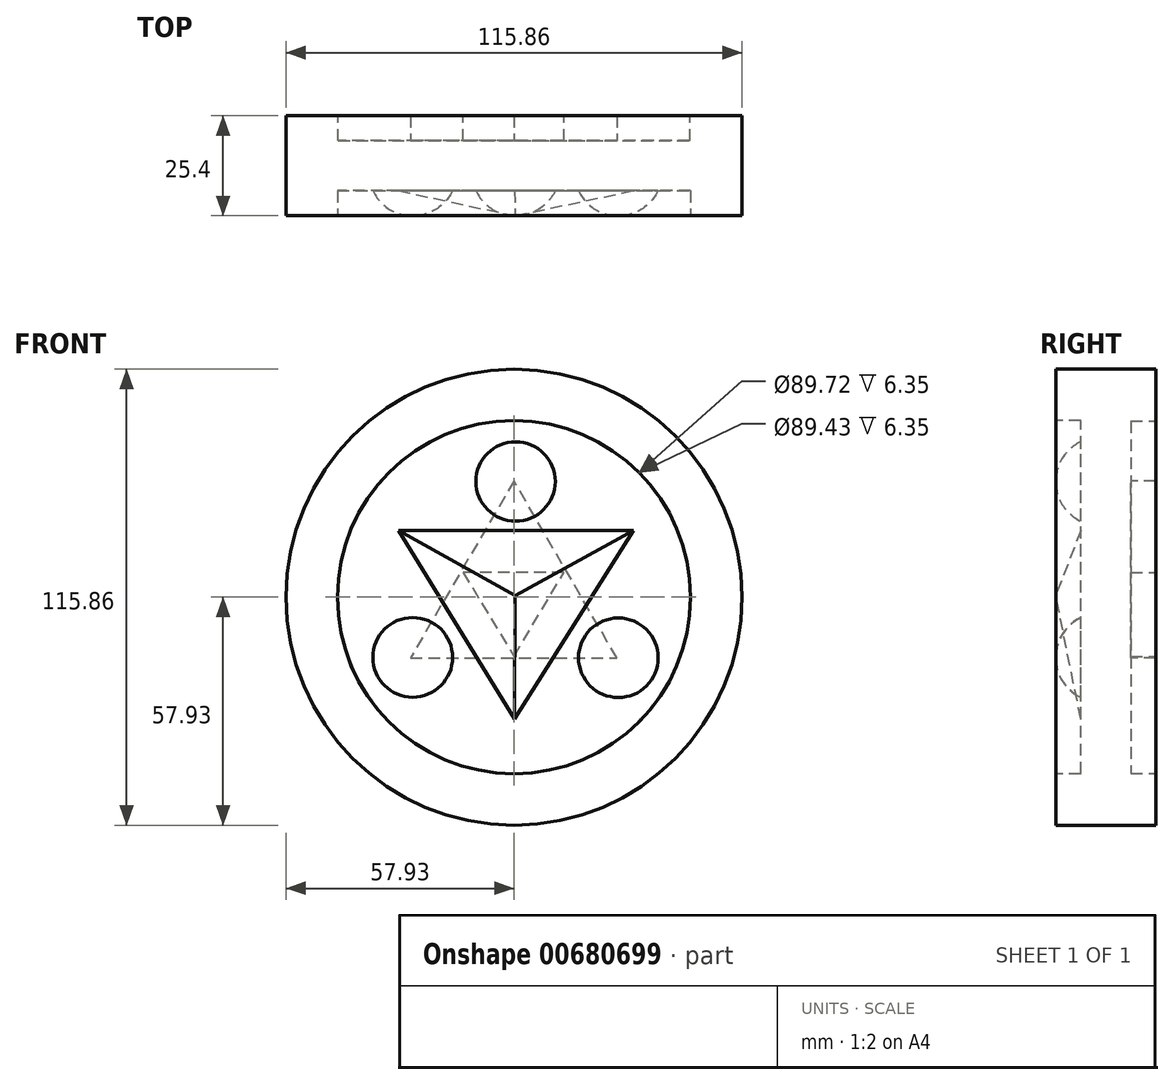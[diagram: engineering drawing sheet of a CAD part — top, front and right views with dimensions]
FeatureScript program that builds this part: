
annotation { "Feature Type Name" : "Feature", "Feature Type Description" : "" }
export const myFeature = defineFeature(function(context is Context, id is Id, definition is map)
    precondition{}
    {
        {
            var Q0;
            Q0=qCreatedBy(makeId("Front.planeOp"),FACE);
            var sketch = newSketch(context, id + "F0", { "sketchPlane" : qUnion([Q0])});
            skCircle(sketch, "E0", {"center": v(0, 0) * mm, "radius": 57.93 * mm});
            skCircle(sketch, "E1", {"center": v(0, 0) * mm, "radius": 45.24 * mm});
            skLineSegment(sketch, "E2", {"start": v(-24.01, 26.9) * mm, "end": v(-4.53, 1.77) * mm});
            skLineSegment(sketch, "E3", {"start": v(-4.53, 1.77) * mm, "end": v(-36.03, 4.88) * mm});
            skLineSegment(sketch, "E4", {"start": v(-36.03, 4.88) * mm, "end": v(-24.01, 26.9) * mm});
            skCircle(sketch, "E5", {"center": v(0, 29.6) * mm, "radius": 10.34 * mm});
            skLineSegment(sketch, "E6", {"start": v(4.46, 1.76) * mm, "end": v(24, 26.88) * mm});
            skLineSegment(sketch, "E7", {"start": v(24, 26.88) * mm, "end": v(36.16, 4.84) * mm});
            skLineSegment(sketch, "E8", {"start": v(36.16, 4.84) * mm, "end": v(4.46, 1.76) * mm});
            skLineSegment(sketch, "E9", {"start": v(0, -5.39) * mm, "end": v(12.64, -34.5) * mm});
            skLineSegment(sketch, "E10", {"start": v(12.64, -34.5) * mm, "end": v(-12.54, -34.5) * mm});
            skLineSegment(sketch, "E11", {"start": v(-12.54, -34.5) * mm, "end": v(0, -5.39) * mm});
            skCircle(sketch, "E12", {"center": v(-26.13, -15.37) * mm, "radius": 10.23 * mm});
            skCircle(sketch, "E13", {"center": v(26.13, -15.19) * mm, "radius": 9.93 * mm});
            skSolve(sketch);
        }
        {
            var Q0;
            Q0=makeQuery(id+"F0.imprint","IMPRINT",FACE,{"disambiguationData":[TD([[makeQuery(id+"F0.imprint","IMPRINT",EDGE,{"derivedFrom":sQuery(id+"F0.wireOp",EDGE,"E0")}),1.0]])]});
            var Q1;
            Q1=makeQuery(id+"F0.imprint","IMPRINT",FACE,{"disambiguationData":[TD([[makeQuery(id+"F0.imprint","IMPRINT",EDGE,{"derivedFrom":sQuery(id+"F0.wireOp",EDGE,"E1")}),1.0]])]});
            var Q2;
            Q2=makeQuery(id+"F0.imprint","IMPRINT",FACE,{"disambiguationData":[TD([[makeQuery(id+"F0.imprint","IMPRINT",EDGE,{"derivedFrom":sQuery(id+"F0.wireOp",EDGE,"E5")}),1.0]])]});
            var Q3;
            Q3=makeQuery(id+"F0.imprint","IMPRINT",FACE,{"disambiguationData":[TD([[makeQuery(id+"F0.imprint","IMPRINT",EDGE,{"derivedFrom":sQuery(id+"F0.wireOp",EDGE,"E2")}),-1.0]])]});
            var Q4;
            Q4=makeQuery(id+"F0.imprint","IMPRINT",FACE,{"disambiguationData":[TD([[makeQuery(id+"F0.imprint","IMPRINT",EDGE,{"derivedFrom":sQuery(id+"F0.wireOp",EDGE,"E12")}),1.0]])]});
            var Q5;
            Q5=makeQuery(id+"F0.imprint","IMPRINT",FACE,{"disambiguationData":[TD([[makeQuery(id+"F0.imprint","IMPRINT",EDGE,{"derivedFrom":sQuery(id+"F0.wireOp",EDGE,"E9")}),-1.0]])]});
            var Q6;
            Q6=makeQuery(id+"F0.imprint","IMPRINT",FACE,{"disambiguationData":[TD([[makeQuery(id+"F0.imprint","IMPRINT",EDGE,{"derivedFrom":sQuery(id+"F0.wireOp",EDGE,"E13")}),1.0]])]});
            var Q7;
            Q7=makeQuery(id+"F0.imprint","IMPRINT",FACE,{"disambiguationData":[TD([[makeQuery(id+"F0.imprint","IMPRINT",EDGE,{"derivedFrom":sQuery(id+"F0.wireOp",EDGE,"E6")}),-1.0]])]});
            extrude(context, id + "F1", {"entities" : qUnion([Q0, Q1, Q2, Q3, Q4, Q5, Q6, Q7]), "depth" : 12.7 * mm, "offsetDistance" : 25.4 * mm});
        }
        {
            var Q0;
            Q0=makeQuery(id+"F1.opExtrude","CAP_FACE",FACE,{"disambiguationData":[OSD([sQuery(id+"F0.wireOp",EDGE,"E0")])],"isStart":true});
            extrude(context, id + "F2", {"entities" : qUnion([Q0]), "operationType" : NewBodyOperationType.ADD, "depth" : 12.7 * mm, "offsetDistance" : 25.4 * mm});
        }
        {
            var Q0;
            Q0=makeQuery(id+"F1.opExtrude","CAP_FACE",FACE,{"disambiguationData":[OSD([sQuery(id+"F0.wireOp",EDGE,"E0")])],"isStart":false});
            var sketch = newSketch(context, id + "F3", { "sketchPlane" : qUnion([Q0])});
            skCircle(sketch, "E14", {"center": v(0, 0) * mm, "radius": 44.86 * mm});
            skSolve(sketch);
        }
        {
            var Q0;
            Q0=makeQuery(id+"F3.imprint","IMPRINT",FACE,{"disambiguationData":[TD([[makeQuery(id+"F3.imprint","IMPRINT",EDGE,{"derivedFrom":sQuery(id+"F3.wireOp",EDGE,"E14")}),1.0]])]});
            extrude(context, id + "F4", {"entities" : qUnion([Q0]), "operationType" : NewBodyOperationType.REMOVE, "oppositeDirection" : true, "depth" : 6.35 * mm, "offsetDistance" : 25.4 * mm});
        }
        {
            var Q0;
            Q0=makeQuery(id+"F2.opExtrude","CAP_FACE",FACE,{"disambiguationData":[OSD([sQuery(id+"F0.wireOp",EDGE,"E0")])],"isStart":false});
            var sketch = newSketch(context, id + "F5", { "sketchPlane" : qUnion([Q0])});
            skCircle(sketch, "E15", {"center": v(0, 0) * mm, "radius": 44.72 * mm});
            skSolve(sketch);
        }
        {
            var Q0;
            Q0=makeQuery(id+"F5.imprint","IMPRINT",FACE,{"disambiguationData":[TD([[makeQuery(id+"F5.imprint","IMPRINT",EDGE,{"derivedFrom":sQuery(id+"F5.wireOp",EDGE,"E15")}),1.0]])]});
            extrude(context, id + "F6", {"entities" : qUnion([Q0]), "operationType" : NewBodyOperationType.REMOVE, "oppositeDirection" : true, "depth" : 6.35 * mm, "offsetDistance" : 25.4 * mm});
        }
        {
            var Q0;
            Q0=makeQuery(id+"F6.boolean.opBoolean","COPY",FACE,{"derivedFrom":makeQuery(id+"F6.opExtrude","CAP_FACE",FACE,{"disambiguationData":[OSD([sQuery(id+"F5.wireOp",EDGE,"E15")])],"isStart":false})});
            var sketch = newSketch(context, id + "F7", { "sketchPlane" : qUnion([Q0])});
            skLineSegment(sketch, "E16", {"start": v(0, 29.52) * mm, "end": v(26.34, -15.44) * mm});
            skLineSegment(sketch, "E17", {"start": v(26.34, -15.44) * mm, "end": v(-26.11, -15.44) * mm});
            skLineSegment(sketch, "E18", {"start": v(-26.11, -15.44) * mm, "end": v(0, 29.52) * mm});
            skLineSegment(sketch, "E19", {"start": v(13.17, 7.04) * mm, "end": v(0.11, -15.44) * mm});
            skLineSegment(sketch, "E20", {"start": v(0.11, -15.44) * mm, "end": v(-13.06, 7.04) * mm});
            skLineSegment(sketch, "E21", {"start": v(-13.06, 7.04) * mm, "end": v(13.17, 7.04) * mm});
            skSolve(sketch);
        }
        {
            var Q0;
            {var subQ3=sQuery(id+"F7.wireOp",EDGE,"E20");Q0=makeQuery(id+"F7.imprint","IMPRINT",FACE,{"disambiguationData":[TD([[makeQuery(id+"F7.imprint","IMPRINT",EDGE,{"derivedFrom":subQ3}),1.0]])]});}
            var Q1;
            Q1=makeQuery(id+"F7.imprint","IMPRINT",FACE,{"disambiguationData":[TD([[makeQuery(id+"F7.imprint","IMPRINT",EDGE,{"derivedFrom":sQuery(id+"F7.wireOp",EDGE,"E19")}),-1.0]])]});
            var Q2;
            {var subQ3=sQuery(id+"F7.wireOp",EDGE,"E21");Q2=makeQuery(id+"F7.imprint","IMPRINT",FACE,{"disambiguationData":[TD([[makeQuery(id+"F7.imprint","IMPRINT",EDGE,{"derivedFrom":subQ3}),1.0]])]});}
            var Q3;
            {var subQ3=sQuery(id+"F7.wireOp",EDGE,"E19");Q3=makeQuery(id+"F7.imprint","IMPRINT",FACE,{"disambiguationData":[TD([[makeQuery(id+"F7.imprint","IMPRINT",EDGE,{"derivedFrom":subQ3}),1.0]])]});}
            extrude(context, id + "F8", {"entities" : qUnion([Q0, Q1, Q2, Q3]), "operationType" : NewBodyOperationType.ADD, "depth" : 6.35 * mm, "offsetDistance" : 25.4 * mm});
        }
        {
            var Q0;
            Q0=makeQuery(id+"F8.opExtrude","CAP_FACE",FACE,{"disambiguationData":[OSD([sQuery(id+"F7.wireOp",EDGE,"E16"),sQuery(id+"F7.wireOp",EDGE,"E17"),sQuery(id+"F7.wireOp",EDGE,"E18")])],"isStart":false});
            var sketch = newSketch(context, id + "F9", { "sketchPlane" : qUnion([Q0])});
            skLineSegment(sketch, "E22", {"start": v(-12.72, 6.35) * mm, "end": v(12.98, 6.35) * mm});
            skLineSegment(sketch, "E23", {"start": v(12.98, 6.35) * mm, "end": v(0, -15) * mm});
            skLineSegment(sketch, "E24", {"start": v(0, -15) * mm, "end": v(-12.72, 6.35) * mm});
            skSolve(sketch);
        }
        {
            var Q0;
            Q0=makeQuery(id+"F9.imprint","IMPRINT",FACE,{"disambiguationData":[TD([[makeQuery(id+"F9.imprint","IMPRINT",EDGE,{"derivedFrom":sQuery(id+"F9.wireOp",EDGE,"E22")}),-1.0]])]});
            extrude(context, id + "F10", {"entities" : qUnion([Q0]), "operationType" : NewBodyOperationType.REMOVE, "oppositeDirection" : true, "depth" : 6.35 * mm, "offsetDistance" : 25.4 * mm});
        }
        {
            var Q0;
            Q0=makeQuery(id+"F4.boolean.opBoolean","COPY",FACE,{"derivedFrom":makeQuery(id+"F4.opExtrude","CAP_FACE",FACE,{"disambiguationData":[OSD([sQuery(id+"F3.wireOp",EDGE,"E14")])],"isStart":false})});
            var sketch = newSketch(context, id + "F11", { "sketchPlane" : qUnion([Q0])});
            skCircle(sketch, "E25", {"center": v(0.4, 29.4) * mm, "radius": 10.09 * mm});
            skCircle(sketch, "E26", {"center": v(26.5, -15.38) * mm, "radius": 10.1 * mm});
            skCircle(sketch, "E27", {"center": v(-25.73, -15.3) * mm, "radius": 10.13 * mm});
            skLineSegment(sketch, "E28", {"start": v(30.51, 17.07) * mm, "end": v(-29.6, 17.07) * mm});
            skLineSegment(sketch, "E29", {"start": v(-29.6, 17.07) * mm, "end": v(0.15, -31.13) * mm});
            skLineSegment(sketch, "E30", {"start": v(0.15, -31.13) * mm, "end": v(30.51, 17.07) * mm});
            skSolve(sketch);
        }
        {
            var Q0;
            Q0=makeQuery(id+"F11.imprint","IMPRINT",FACE,{"disambiguationData":[TD([[makeQuery(id+"F11.imprint","IMPRINT",EDGE,{"derivedFrom":sQuery(id+"F11.wireOp",EDGE,"E25")}),1.0]])]});
            var Q1;
            Q1=makeQuery(id+"F11.imprint","IMPRINT",FACE,{"disambiguationData":[TD([[makeQuery(id+"F11.imprint","IMPRINT",EDGE,{"derivedFrom":sQuery(id+"F11.wireOp",EDGE,"E26")}),1.0]])]});
            var Q2;
            Q2=makeQuery(id+"F11.imprint","IMPRINT",FACE,{"disambiguationData":[TD([[makeQuery(id+"F11.imprint","IMPRINT",EDGE,{"derivedFrom":sQuery(id+"F11.wireOp",EDGE,"E27")}),1.0]])]});
            var Q3;
            Q3=makeQuery(id+"F11.imprint","IMPRINT",FACE,{"disambiguationData":[TD([[makeQuery(id+"F11.imprint","IMPRINT",EDGE,{"derivedFrom":sQuery(id+"F11.wireOp",EDGE,"E28")}),1.0]])]});
            extrude(context, id + "F12", {"entities" : qUnion([Q0, Q1, Q2, Q3]), "operationType" : NewBodyOperationType.ADD, "depth" : 6.35 * mm, "offsetDistance" : 25.4 * mm});
        }
        {
            var Q0;
            Q0=makeQuery(id+"F12.opExtrude","CAP_FACE",FACE,{"disambiguationData":[OSD([sQuery(id+"F11.wireOp",EDGE,"E25")])],"isStart":false});
            fillet(context, id + "F13", {"entities" : qUnion([Q0]), "radius" : 10.92 * mm, "tangentPropagation" : true, "allowEdgeOverflow" : false});
        }
        {
            var Q0;
            Q0=makeQuery(id+"F12.opExtrude","CAP_FACE",FACE,{"disambiguationData":[OSD([sQuery(id+"F11.wireOp",EDGE,"E27")])],"isStart":false});
            fillet(context, id + "F14", {"entities" : qUnion([Q0]), "radius" : 11.05 * mm, "tangentPropagation" : true, "allowEdgeOverflow" : false});
        }
        {
            var Q0;
            Q0=makeQuery(id+"F12.opExtrude","CAP_FACE",FACE,{"disambiguationData":[OSD([sQuery(id+"F11.wireOp",EDGE,"E26")])],"isStart":false});
            fillet(context, id + "F15", {"entities" : qUnion([Q0]), "radius" : 11.05 * mm, "tangentPropagation" : true, "allowEdgeOverflow" : false});
        }
        {
            var Q0;
            Q0=makeQuery(id+"F12.opExtrude","CAP_FACE",FACE,{"disambiguationData":[OSD([sQuery(id+"F11.wireOp",EDGE,"E28"),sQuery(id+"F11.wireOp",EDGE,"E29"),sQuery(id+"F11.wireOp",EDGE,"E30")])],"isStart":false});
            chamfer(context, id + "F16", {"entities" : qUnion([Q0]), "chamferType" : ChamferType.OFFSET_ANGLE, "width" : 16.66 * mm, "oppositeDirection" : false, "angle" : 21 * degree, "tangentPropagation" : true});
        }
    });
